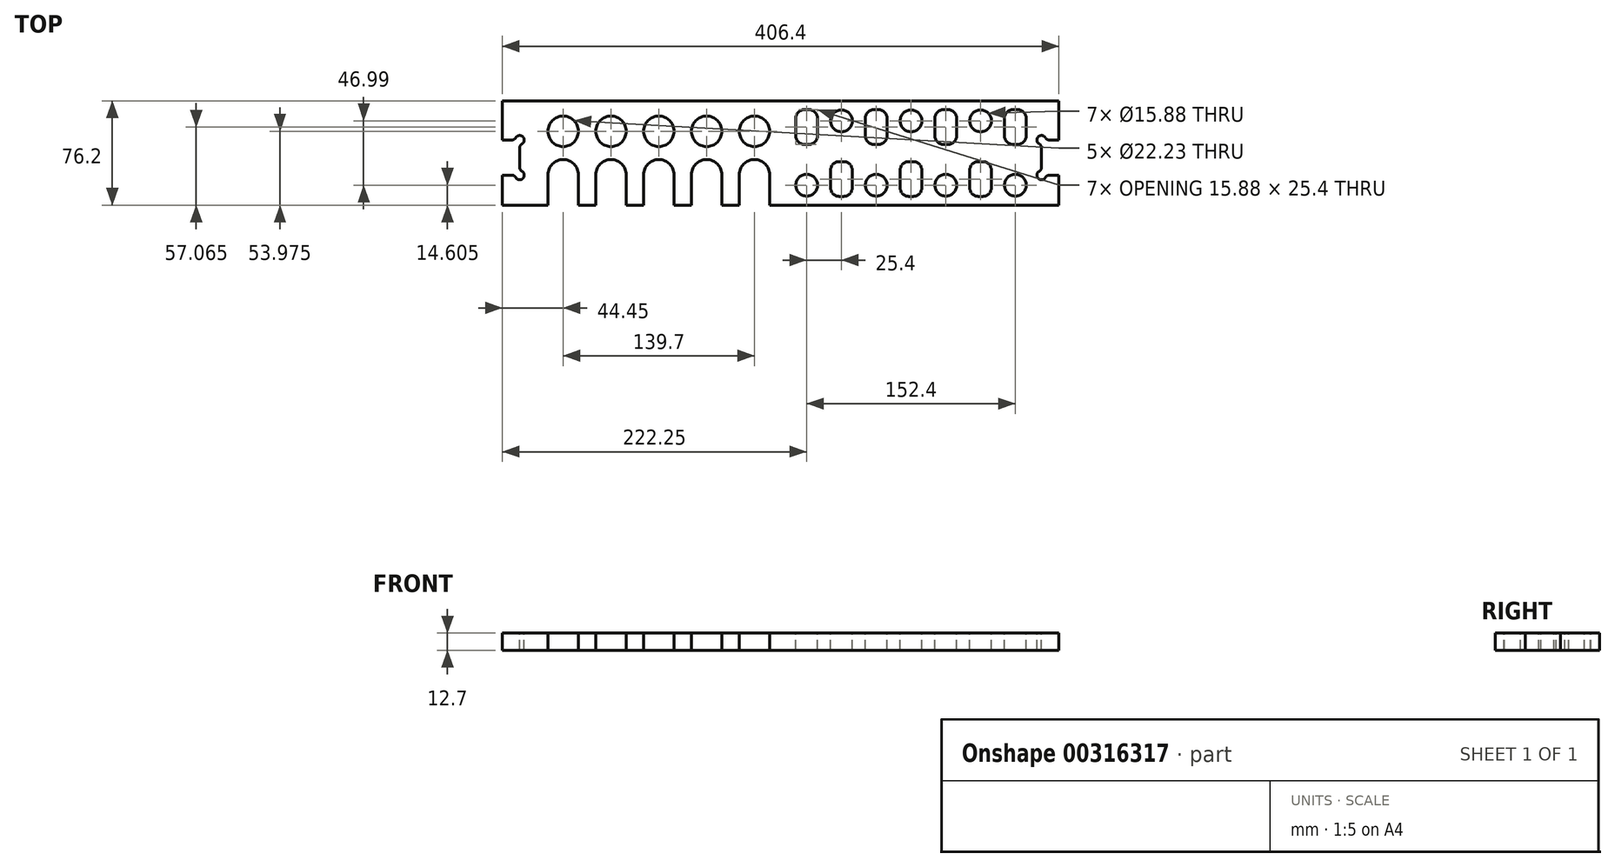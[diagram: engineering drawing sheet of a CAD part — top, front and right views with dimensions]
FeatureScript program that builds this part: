
annotation { "Feature Type Name" : "Feature", "Feature Type Description" : "" }
export const myFeature = defineFeature(function(context is Context, id is Id, definition is map)
    precondition{}
    {
        {
            var Q0;
            Q0=qCreatedBy(makeId("Top.planeOp"),FACE);
            var sketch = newSketch(context, id + "F0", { "sketchPlane" : qUnion([Q0])});
            skLineSegment(sketch, "E0.bottom", {"start": v(0, 0) * mm, "end": v(406.4, 0) * mm});
            skLineSegment(sketch, "E0.top", {"start": v(0, 76.2) * mm, "end": v(406.4, 76.2) * mm});
            skLineSegment(sketch, "E0.left", {"start": v(0, 0) * mm, "end": v(0, 76.2) * mm});
            skLineSegment(sketch, "E0.right", {"start": v(406.4, 0) * mm, "end": v(406.4, 76.2) * mm});
            skSolve(sketch);
        }
        {
            var Q0;
            Q0 = qSketchRegion(id + "F0", true);
            extrude(context, id + "F1", {"entities" : qUnion([Q0]), "depth" : 12.7 * mm});
        }
        {
            var Q0;
            Q0=makeQuery(id+"F1.opExtrude","CAP_FACE",FACE,{"disambiguationData":[OSD([sQuery(id+"F0.wireOp",EDGE,"E0.bottom"),sQuery(id+"F0.wireOp",EDGE,"E0.top"),sQuery(id+"F0.wireOp",EDGE,"E0.left"),sQuery(id+"F0.wireOp",EDGE,"E0.right")])],"isStart":false});
            var sketch = newSketch(context, id + "F2", { "sketchPlane" : qUnion([Q0])});
            skLineSegment(sketch, "E1", {"start": v(0, 38.1) * mm, "end": v(103.18, 38.1) * mm, "construction": true});
            skLineSegment(sketch, "E2", {"start": v(203.2, 76.2) * mm, "end": v(203.2, 0) * mm, "construction": true});
            skLineSegment(sketch, "E3.bottom", {"start": v(0, 47.63) * mm, "end": v(7.05, 47.63) * mm});
            skLineSegment(sketch, "E3.top", {"start": v(0, 21.84) * mm, "end": v(7.05, 21.84) * mm});
            skLineSegment(sketch, "E3.left", {"start": v(0, 47.63) * mm, "end": v(0, 21.84) * mm});
            skLineSegment(sketch, "E3.right", {"start": v(12.7, 41.98) * mm, "end": v(12.7, 27.49) * mm});
            skArc(sketch, "E4", {"start": v(14.32, 44.75) * mm, "mid": v(15.03, 49.96) * mm, "end": v(9.82, 49.24) * mm});
            skArc(sketch, "E5", {"start": v(9.82, 20.23) * mm, "mid": v(15.03, 19.5) * mm, "end": v(14.32, 24.72) * mm});
            skPoint(sketch, "E6.visualSharp", {"position": v(9.4, 47.63) * mm});
            skArc(sketch, "E6.filletArc", {"start": v(7.05, 47.63) * mm, "mid": v(8.66, 48.06) * mm, "end": v(9.82, 49.24) * mm});
            skPoint(sketch, "E7.visualSharp", {"position": v(9.4, 21.84) * mm});
            skArc(sketch, "E7.filletArc", {"start": v(9.82, 20.23) * mm, "mid": v(8.66, 21.4) * mm, "end": v(7.05, 21.84) * mm});
            skPoint(sketch, "E8.visualSharp", {"position": v(12.7, 44.32) * mm});
            skArc(sketch, "E8.filletArc", {"start": v(14.32, 44.75) * mm, "mid": v(13.13, 43.58) * mm, "end": v(12.7, 41.98) * mm});
            skPoint(sketch, "E9.visualSharp", {"position": v(12.7, 25.15) * mm});
            skArc(sketch, "E9.filletArc", {"start": v(12.7, 27.49) * mm, "mid": v(13.13, 25.89) * mm, "end": v(14.32, 24.72) * mm});
            skArc(sketch, "E10.MirrorCS", {"start": v(393.7, 27.49) * mm, "mid": v(393.27, 25.89) * mm, "end": v(392.08, 24.72) * mm});
            skArc(sketch, "E11.MirrorCS", {"start": v(399.35, 47.63) * mm, "mid": v(397.74, 48.06) * mm, "end": v(396.58, 49.24) * mm});
            skArc(sketch, "E12.MirrorCS", {"start": v(392.08, 44.75) * mm, "mid": v(391.37, 49.96) * mm, "end": v(396.58, 49.24) * mm});
            skLineSegment(sketch, "E13.MirrorCS", {"start": v(406.4, 47.63) * mm, "end": v(399.35, 47.63) * mm});
            skArc(sketch, "E14.MirrorCS", {"start": v(396.58, 20.23) * mm, "mid": v(397.74, 21.4) * mm, "end": v(399.35, 21.84) * mm});
            skArc(sketch, "E15.MirrorCS", {"start": v(392.08, 44.75) * mm, "mid": v(393.27, 43.58) * mm, "end": v(393.7, 41.98) * mm});
            skLineSegment(sketch, "E16.MirrorCS", {"start": v(406.4, 21.84) * mm, "end": v(399.35, 21.84) * mm});
            skPoint(sketch, "E17.MirrorP", {"position": v(397, 47.63) * mm});
            skPoint(sketch, "E18.MirrorP", {"position": v(393.7, 25.15) * mm});
            skArc(sketch, "E19.MirrorCS", {"start": v(396.58, 20.23) * mm, "mid": v(391.37, 19.5) * mm, "end": v(392.08, 24.72) * mm});
            skPoint(sketch, "E20.MirrorP", {"position": v(393.7, 44.32) * mm});
            skPoint(sketch, "E21.MirrorP", {"position": v(397, 21.84) * mm});
            skLineSegment(sketch, "E22.MirrorCS", {"start": v(393.7, 41.98) * mm, "end": v(393.7, 27.49) * mm});
            skLineSegment(sketch, "E23.MirrorCS", {"start": v(406.4, 47.63) * mm, "end": v(406.4, 21.84) * mm});
            skSolve(sketch);
        }
        {
            var Q0;
            Q0 = qSketchRegion(id + "F2", true);
            extrude(context, id + "F3", {"entities" : qUnion([Q0]), "operationType" : NewBodyOperationType.REMOVE, "oppositeDirection" : true, "depth" : 25.4 * mm});
        }
        {
            var Q0;
            Q0=makeQuery(id+"F1.opExtrude","CAP_FACE",FACE,{"disambiguationData":[OSD([sQuery(id+"F0.wireOp",EDGE,"E0.bottom"),sQuery(id+"F0.wireOp",EDGE,"E0.top"),sQuery(id+"F0.wireOp",EDGE,"E0.left"),sQuery(id+"F0.wireOp",EDGE,"E0.right")])],"isStart":false});
            var sketch = newSketch(context, id + "F4", { "sketchPlane" : qUnion([Q0])});
            skLineSegment(sketch, "E24", {"start": v(12.7, 34.73) * mm, "end": v(393.7, 34.73) * mm, "construction": true});
            skLineSegment(sketch, "E25", {"start": v(203.2, 76.2) * mm, "end": v(203.2, 0) * mm, "construction": true});
            skLineSegment(sketch, "E26", {"start": v(0, 53.97) * mm, "end": v(406.4, 53.98) * mm, "construction": true});
            skLineSegment(sketch, "E27", {"start": v(0, 22.23) * mm, "end": v(406.4, 22.23) * mm, "construction": true});
            skCircle(sketch, "E28", {"center": v(44.45, 53.98) * mm, "radius": 11.11 * mm});
            skArc(sketch, "E29.0.1.0", {"start": v(55.56, 22.23) * mm, "mid": v(44.45, 33.34) * mm, "end": v(33.34, 22.23) * mm});
            skLineSegment(sketch, "E29.direction1", {"start": v(44.45, 53.97) * mm, "end": v(82.69, 53.97) * mm, "construction": true});
            skLineSegment(sketch, "E30", {"start": v(33.34, 22.23) * mm, "end": v(33.34, 0) * mm});
            skLineSegment(sketch, "E31", {"start": v(33.34, 0) * mm, "end": v(33.34, -12.15) * mm});
            skLineSegment(sketch, "E32", {"start": v(55.56, 22.23) * mm, "end": v(55.56, -12.15) * mm});
            skLineSegment(sketch, "E33", {"start": v(55.56, -12.15) * mm, "end": v(33.34, -12.15) * mm});
            skLineSegment(sketch, "E34", {"start": v(215.9, 17.27) * mm, "end": v(406.4, 17.27) * mm, "construction": true});
            skLineSegment(sketch, "E35", {"start": v(215.9, 14.6) * mm, "end": v(406.4, 14.6) * mm, "construction": true});
            skLineSegment(sketch, "E36", {"start": v(406.4, 61.6) * mm, "end": v(203.2, 61.6) * mm, "construction": true});
            skCircle(sketch, "E37", {"center": v(222.25, 14.6) * mm, "radius": 7.94 * mm});
            skCircle(sketch, "E38", {"center": v(247.65, 61.6) * mm, "radius": 7.94 * mm});
            skLineSegment(sketch, "E39.bottom", {"start": v(223.84, 44.36) * mm, "end": v(220.66, 44.36) * mm});
            skLineSegment(sketch, "E39.top", {"start": v(223.84, 69.76) * mm, "end": v(220.66, 69.76) * mm});
            skLineSegment(sketch, "E39.left", {"start": v(230.19, 50.71) * mm, "end": v(230.19, 63.41) * mm});
            skLineSegment(sketch, "E39.right", {"start": v(214.31, 50.71) * mm, "end": v(214.31, 63.41) * mm});
            skPoint(sketch, "E39.middle", {"position": v(222.25, 57.06) * mm});
            skPoint(sketch, "E40.visualSharp", {"position": v(214.31, 69.76) * mm});
            skArc(sketch, "E40.filletArc", {"start": v(220.66, 69.76) * mm, "mid": v(216.17, 67.9) * mm, "end": v(214.31, 63.41) * mm});
            skPoint(sketch, "E41.visualSharp", {"position": v(230.19, 69.76) * mm});
            skArc(sketch, "E41.filletArc", {"start": v(230.19, 63.41) * mm, "mid": v(228.33, 67.9) * mm, "end": v(223.84, 69.76) * mm});
            skPoint(sketch, "E42.visualSharp", {"position": v(230.19, 44.36) * mm});
            skArc(sketch, "E42.filletArc", {"start": v(223.84, 44.36) * mm, "mid": v(228.33, 46.22) * mm, "end": v(230.19, 50.71) * mm});
            skPoint(sketch, "E43.visualSharp", {"position": v(214.31, 44.36) * mm});
            skArc(sketch, "E43.filletArc", {"start": v(214.31, 50.71) * mm, "mid": v(216.17, 46.22) * mm, "end": v(220.66, 44.36) * mm});
            skLineSegment(sketch, "E44.bottom", {"start": v(249.24, 6.43) * mm, "end": v(246.06, 6.43) * mm});
            skLineSegment(sketch, "E44.top", {"start": v(249.24, 31.83) * mm, "end": v(246.06, 31.83) * mm});
            skLineSegment(sketch, "E44.left", {"start": v(255.59, 12.78) * mm, "end": v(255.59, 25.48) * mm});
            skLineSegment(sketch, "E44.right", {"start": v(239.71, 12.78) * mm, "end": v(239.71, 25.48) * mm});
            skPoint(sketch, "E44.middle", {"position": v(247.65, 19.13) * mm});
            skPoint(sketch, "E45.visualSharp", {"position": v(239.71, 31.83) * mm});
            skArc(sketch, "E45.filletArc", {"start": v(246.06, 31.83) * mm, "mid": v(241.57, 29.97) * mm, "end": v(239.71, 25.48) * mm});
            skPoint(sketch, "E46.visualSharp", {"position": v(255.59, 31.83) * mm});
            skArc(sketch, "E46.filletArc", {"start": v(255.59, 25.48) * mm, "mid": v(253.73, 29.97) * mm, "end": v(249.24, 31.83) * mm});
            skPoint(sketch, "E47.visualSharp", {"position": v(255.59, 6.43) * mm});
            skArc(sketch, "E47.filletArc", {"start": v(249.24, 6.43) * mm, "mid": v(253.73, 8.29) * mm, "end": v(255.59, 12.78) * mm});
            skPoint(sketch, "E48.visualSharp", {"position": v(239.71, 6.43) * mm});
            skArc(sketch, "E48.filletArc", {"start": v(239.71, 12.78) * mm, "mid": v(241.57, 8.29) * mm, "end": v(246.06, 6.43) * mm});
            skArc(sketch, "E49.1.0.0", {"start": v(300.04, 6.43) * mm, "mid": v(304.53, 8.29) * mm, "end": v(306.39, 12.78) * mm});
            skPoint(sketch, "E49.1.0.1", {"position": v(298.45, 19.13) * mm});
            skLineSegment(sketch, "E49.1.0.2", {"start": v(265.11, 50.71) * mm, "end": v(265.11, 63.41) * mm});
            skLineSegment(sketch, "E49.1.0.3", {"start": v(290.51, 12.78) * mm, "end": v(290.51, 25.48) * mm});
            skPoint(sketch, "E49.1.0.4", {"position": v(306.39, 31.83) * mm});
            skPoint(sketch, "E49.1.0.5", {"position": v(280.99, 44.36) * mm});
            skArc(sketch, "E49.1.0.6", {"start": v(274.64, 44.36) * mm, "mid": v(279.13, 46.22) * mm, "end": v(280.99, 50.71) * mm});
            skPoint(sketch, "E49.1.0.7", {"position": v(290.51, 6.43) * mm});
            skPoint(sketch, "E49.1.0.8", {"position": v(273.05, 57.06) * mm});
            skLineSegment(sketch, "E49.1.0.9", {"start": v(306.39, 12.78) * mm, "end": v(306.39, 25.48) * mm});
            skPoint(sketch, "E49.1.0.10", {"position": v(290.51, 31.83) * mm});
            skLineSegment(sketch, "E49.1.0.11", {"start": v(280.99, 50.71) * mm, "end": v(280.99, 63.41) * mm});
            skArc(sketch, "E49.1.0.12", {"start": v(296.86, 31.83) * mm, "mid": v(292.37, 29.97) * mm, "end": v(290.51, 25.48) * mm});
            skPoint(sketch, "E49.1.0.13", {"position": v(265.11, 69.76) * mm});
            skArc(sketch, "E49.1.0.14", {"start": v(265.11, 50.71) * mm, "mid": v(266.97, 46.22) * mm, "end": v(271.46, 44.36) * mm});
            skPoint(sketch, "E49.1.0.15", {"position": v(280.99, 69.76) * mm});
            skCircle(sketch, "E49.1.0.16", {"center": v(298.45, 61.6) * mm, "radius": 7.94 * mm});
            skPoint(sketch, "E49.1.0.17", {"position": v(265.11, 44.36) * mm});
            skArc(sketch, "E49.1.0.18", {"start": v(271.46, 69.76) * mm, "mid": v(266.97, 67.9) * mm, "end": v(265.11, 63.41) * mm});
            skArc(sketch, "E49.1.0.19", {"start": v(306.39, 25.48) * mm, "mid": v(304.53, 29.97) * mm, "end": v(300.04, 31.83) * mm});
            skPoint(sketch, "E49.1.0.20", {"position": v(306.39, 6.43) * mm});
            skCircle(sketch, "E49.1.0.21", {"center": v(273.05, 14.6) * mm, "radius": 7.94 * mm});
            skArc(sketch, "E49.1.0.22", {"start": v(280.99, 63.41) * mm, "mid": v(279.13, 67.9) * mm, "end": v(274.64, 69.76) * mm});
            skArc(sketch, "E49.1.0.23", {"start": v(290.51, 12.78) * mm, "mid": v(292.37, 8.29) * mm, "end": v(296.86, 6.43) * mm});
            skLineSegment(sketch, "E49.1.0.24", {"start": v(300.04, 6.43) * mm, "end": v(296.86, 6.43) * mm});
            skLineSegment(sketch, "E49.1.0.25", {"start": v(274.64, 44.36) * mm, "end": v(271.46, 44.36) * mm});
            skLineSegment(sketch, "E49.1.0.26", {"start": v(300.04, 31.83) * mm, "end": v(296.86, 31.83) * mm});
            skLineSegment(sketch, "E49.1.0.27", {"start": v(274.64, 69.76) * mm, "end": v(271.46, 69.76) * mm});
            skArc(sketch, "E49.2.0.0", {"start": v(350.84, 6.43) * mm, "mid": v(355.33, 8.29) * mm, "end": v(357.19, 12.78) * mm});
            skPoint(sketch, "E49.2.0.1", {"position": v(349.25, 19.13) * mm});
            skLineSegment(sketch, "E49.2.0.2", {"start": v(315.91, 50.71) * mm, "end": v(315.91, 63.41) * mm});
            skLineSegment(sketch, "E49.2.0.3", {"start": v(341.31, 12.78) * mm, "end": v(341.31, 25.48) * mm});
            skPoint(sketch, "E49.2.0.4", {"position": v(357.19, 31.83) * mm});
            skPoint(sketch, "E49.2.0.5", {"position": v(331.79, 44.36) * mm});
            skArc(sketch, "E49.2.0.6", {"start": v(325.44, 44.36) * mm, "mid": v(329.93, 46.22) * mm, "end": v(331.79, 50.71) * mm});
            skPoint(sketch, "E49.2.0.7", {"position": v(341.31, 6.43) * mm});
            skPoint(sketch, "E49.2.0.8", {"position": v(323.85, 57.06) * mm});
            skLineSegment(sketch, "E49.2.0.9", {"start": v(357.19, 12.78) * mm, "end": v(357.19, 25.48) * mm});
            skPoint(sketch, "E49.2.0.10", {"position": v(341.31, 31.83) * mm});
            skLineSegment(sketch, "E49.2.0.11", {"start": v(331.79, 50.71) * mm, "end": v(331.79, 63.41) * mm});
            skArc(sketch, "E49.2.0.12", {"start": v(347.66, 31.83) * mm, "mid": v(343.17, 29.97) * mm, "end": v(341.31, 25.48) * mm});
            skPoint(sketch, "E49.2.0.13", {"position": v(315.91, 69.76) * mm});
            skArc(sketch, "E49.2.0.14", {"start": v(315.91, 50.71) * mm, "mid": v(317.77, 46.22) * mm, "end": v(322.26, 44.36) * mm});
            skPoint(sketch, "E49.2.0.15", {"position": v(331.79, 69.76) * mm});
            skCircle(sketch, "E49.2.0.16", {"center": v(349.25, 61.6) * mm, "radius": 7.94 * mm});
            skPoint(sketch, "E49.2.0.17", {"position": v(315.91, 44.36) * mm});
            skArc(sketch, "E49.2.0.18", {"start": v(322.26, 69.76) * mm, "mid": v(317.77, 67.9) * mm, "end": v(315.91, 63.41) * mm});
            skArc(sketch, "E49.2.0.19", {"start": v(357.19, 25.48) * mm, "mid": v(355.33, 29.97) * mm, "end": v(350.84, 31.83) * mm});
            skPoint(sketch, "E49.2.0.20", {"position": v(357.19, 6.43) * mm});
            skCircle(sketch, "E49.2.0.21", {"center": v(323.85, 14.6) * mm, "radius": 7.94 * mm});
            skArc(sketch, "E49.2.0.22", {"start": v(331.79, 63.41) * mm, "mid": v(329.93, 67.9) * mm, "end": v(325.44, 69.76) * mm});
            skArc(sketch, "E49.2.0.23", {"start": v(341.31, 12.78) * mm, "mid": v(343.17, 8.29) * mm, "end": v(347.66, 6.43) * mm});
            skLineSegment(sketch, "E49.2.0.24", {"start": v(350.84, 6.43) * mm, "end": v(347.66, 6.43) * mm});
            skLineSegment(sketch, "E49.2.0.25", {"start": v(325.44, 44.36) * mm, "end": v(322.26, 44.36) * mm});
            skLineSegment(sketch, "E49.2.0.26", {"start": v(350.84, 31.83) * mm, "end": v(347.66, 31.83) * mm});
            skLineSegment(sketch, "E49.2.0.27", {"start": v(325.44, 69.76) * mm, "end": v(322.26, 69.76) * mm});
            skLineSegment(sketch, "E49.3.0.2", {"start": v(366.71, 50.71) * mm, "end": v(366.71, 63.41) * mm});
            skPoint(sketch, "E49.3.0.5", {"position": v(382.59, 44.36) * mm});
            skArc(sketch, "E49.3.0.6", {"start": v(376.24, 44.36) * mm, "mid": v(380.73, 46.22) * mm, "end": v(382.59, 50.71) * mm});
            skPoint(sketch, "E49.3.0.8", {"position": v(374.65, 57.06) * mm});
            skLineSegment(sketch, "E49.3.0.11", {"start": v(382.59, 50.71) * mm, "end": v(382.59, 63.41) * mm});
            skPoint(sketch, "E49.3.0.13", {"position": v(366.71, 69.76) * mm});
            skArc(sketch, "E49.3.0.14", {"start": v(366.71, 50.71) * mm, "mid": v(368.57, 46.22) * mm, "end": v(373.06, 44.36) * mm});
            skPoint(sketch, "E49.3.0.15", {"position": v(382.59, 69.76) * mm});
            skPoint(sketch, "E49.3.0.17", {"position": v(366.71, 44.36) * mm});
            skArc(sketch, "E49.3.0.18", {"start": v(373.06, 69.76) * mm, "mid": v(368.57, 67.9) * mm, "end": v(366.71, 63.41) * mm});
            skCircle(sketch, "E49.3.0.21", {"center": v(374.65, 14.6) * mm, "radius": 7.94 * mm});
            skArc(sketch, "E49.3.0.22", {"start": v(382.59, 63.41) * mm, "mid": v(380.73, 67.9) * mm, "end": v(376.24, 69.76) * mm});
            skLineSegment(sketch, "E49.3.0.25", {"start": v(376.24, 44.36) * mm, "end": v(373.06, 44.36) * mm});
            skLineSegment(sketch, "E49.3.0.27", {"start": v(376.24, 69.76) * mm, "end": v(373.06, 69.76) * mm});
            skLineSegment(sketch, "E49.direction1", {"start": v(222.25, 14.6) * mm, "end": v(273.05, 14.6) * mm, "construction": true});
            skArc(sketch, "E50.1.0.0", {"start": v(90.49, 22.23) * mm, "mid": v(79.38, 33.34) * mm, "end": v(68.26, 22.23) * mm});
            skCircle(sketch, "E50.1.0.1", {"center": v(79.38, 53.98) * mm, "radius": 11.11 * mm});
            skLineSegment(sketch, "E50.1.0.2", {"start": v(68.26, 22.23) * mm, "end": v(68.26, 0) * mm});
            skLineSegment(sketch, "E50.1.0.3", {"start": v(90.49, 22.23) * mm, "end": v(90.49, -12.15) * mm});
            skLineSegment(sketch, "E50.1.0.4", {"start": v(68.26, 0) * mm, "end": v(68.26, -12.15) * mm});
            skLineSegment(sketch, "E50.1.0.5", {"start": v(90.49, -12.15) * mm, "end": v(68.26, -12.15) * mm});
            skArc(sketch, "E50.2.0.0", {"start": v(125.41, 22.23) * mm, "mid": v(114.3, 33.34) * mm, "end": v(103.19, 22.23) * mm});
            skCircle(sketch, "E50.2.0.1", {"center": v(114.3, 53.98) * mm, "radius": 11.11 * mm});
            skLineSegment(sketch, "E50.2.0.2", {"start": v(103.19, 22.23) * mm, "end": v(103.19, 0) * mm});
            skLineSegment(sketch, "E50.2.0.3", {"start": v(125.41, 22.23) * mm, "end": v(125.41, -12.15) * mm});
            skLineSegment(sketch, "E50.2.0.4", {"start": v(103.19, 0) * mm, "end": v(103.19, -12.15) * mm});
            skLineSegment(sketch, "E50.2.0.5", {"start": v(125.41, -12.15) * mm, "end": v(103.19, -12.15) * mm});
            skArc(sketch, "E50.3.0.0", {"start": v(160.34, 22.23) * mm, "mid": v(149.23, 33.34) * mm, "end": v(138.11, 22.23) * mm});
            skCircle(sketch, "E50.3.0.1", {"center": v(149.23, 53.98) * mm, "radius": 11.11 * mm});
            skLineSegment(sketch, "E50.3.0.2", {"start": v(138.11, 22.23) * mm, "end": v(138.11, 0) * mm});
            skLineSegment(sketch, "E50.3.0.3", {"start": v(160.34, 22.23) * mm, "end": v(160.34, -12.15) * mm});
            skLineSegment(sketch, "E50.3.0.4", {"start": v(138.11, 0) * mm, "end": v(138.11, -12.15) * mm});
            skLineSegment(sketch, "E50.3.0.5", {"start": v(160.34, -12.15) * mm, "end": v(138.11, -12.15) * mm});
            skArc(sketch, "E50.4.0.0", {"start": v(195.26, 22.23) * mm, "mid": v(184.15, 33.34) * mm, "end": v(173.04, 22.23) * mm});
            skCircle(sketch, "E50.4.0.1", {"center": v(184.15, 53.98) * mm, "radius": 11.11 * mm});
            skLineSegment(sketch, "E50.4.0.2", {"start": v(173.04, 22.23) * mm, "end": v(173.04, 0) * mm});
            skLineSegment(sketch, "E50.4.0.3", {"start": v(195.26, 22.23) * mm, "end": v(195.26, -12.15) * mm});
            skLineSegment(sketch, "E50.4.0.4", {"start": v(173.04, 0) * mm, "end": v(173.04, -12.15) * mm});
            skLineSegment(sketch, "E50.4.0.5", {"start": v(195.26, -12.15) * mm, "end": v(173.04, -12.15) * mm});
            skLineSegment(sketch, "E50.direction1", {"start": v(33.34, -12.15) * mm, "end": v(68.26, -12.15) * mm, "construction": true});
            skSolve(sketch);
        }
        {
            var Q0;
            Q0 = qSketchRegion(id + "F4", true);
            extrude(context, id + "F5", {"entities" : qUnion([Q0]), "operationType" : NewBodyOperationType.REMOVE, "oppositeDirection" : true, "depth" : 25.4 * mm});
        }
    });
